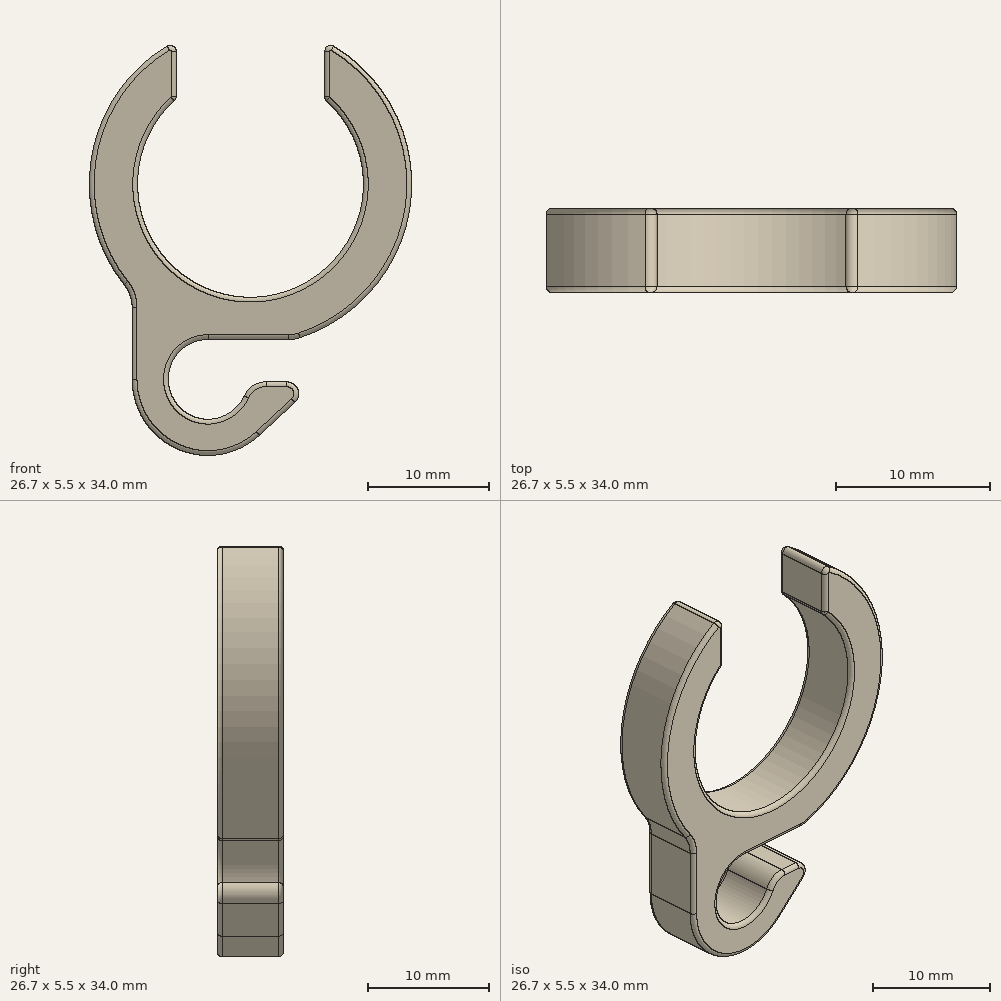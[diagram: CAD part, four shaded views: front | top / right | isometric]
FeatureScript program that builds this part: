
annotation { "Feature Type Name" : "Feature", "Feature Type Description" : "" }
export const myFeature = defineFeature(function(context is Context, id is Id, definition is map)
    precondition{}
    {
        {
            var Q0;
            Q0=qCreatedBy(makeId("Front.planeOp"),FACE);
            var sketch = newSketch(context, id + "F0", { "sketchPlane" : qUnion([Q0])});
            skArc(sketch, "E0", {"start": v(-6.31, 6.9) * mm, "mid": v(0, -9.35) * mm, "end": v(6.31, 6.9) * mm});
            skArc(sketch, "E1", {"start": v(-6.9, 11.42) * mm, "mid": v(-13.14, 2.36) * mm, "end": v(-10.45, -8.3) * mm});
            skLineSegment(sketch, "E2", {"start": v(-6.15, 11) * mm, "end": v(-6.15, 7.27) * mm});
            skLineSegment(sketch, "E3", {"start": v(6.15, 11) * mm, "end": v(6.15, 7.27) * mm});
            skPoint(sketch, "E4.visualSharp", {"position": v(-6.15, 11.85) * mm});
            skArc(sketch, "E4.filletArc", {"start": v(-6.15, 11) * mm, "mid": v(-6.4, 11.43) * mm, "end": v(-6.9, 11.42) * mm});
            skPoint(sketch, "E5.visualSharp", {"position": v(-6.15, 7.04) * mm});
            skArc(sketch, "E5.filletArc", {"start": v(-6.31, 6.9) * mm, "mid": v(-6.2, 7.06) * mm, "end": v(-6.15, 7.27) * mm});
            skPoint(sketch, "E6.visualSharp", {"position": v(6.15, 7.04) * mm});
            skArc(sketch, "E6.filletArc", {"start": v(6.15, 7.27) * mm, "mid": v(6.2, 7.06) * mm, "end": v(6.31, 6.9) * mm});
            skPoint(sketch, "E7.visualSharp", {"position": v(6.15, 11.85) * mm});
            skArc(sketch, "E7.filletArc", {"start": v(6.9, 11.42) * mm, "mid": v(6.4, 11.43) * mm, "end": v(6.15, 11) * mm});
            skLineSegment(sketch, "E8", {"start": v(0.78, -20.77) * mm, "end": v(3.68, -18.08) * mm});
            skArc(sketch, "E9", {"start": v(-3.5, -12.85) * mm, "mid": v(-6.28, -17.93) * mm, "end": v(-0.5, -17.52) * mm});
            skArc(sketch, "E10", {"start": v(-9.8, -16.15) * mm, "mid": v(-6.02, -21.92) * mm, "end": v(0.78, -20.77) * mm});
            skLineSegment(sketch, "E11", {"start": v(1.32, -16.35) * mm, "end": v(3, -16.35) * mm});
            skArc(sketch, "E12.filletArc", {"start": v(3.68, -18.08) * mm, "mid": v(3.93, -16.98) * mm, "end": v(3, -16.35) * mm});
            skLineSegment(sketch, "E13", {"start": v(-3.5, -12.85) * mm, "end": v(3.18, -12.85) * mm});
            skArc(sketch, "E14.trimOffspring", {"start": v(4.1, -12.7) * mm, "mid": v(13.26, -1.54) * mm, "end": v(6.9, 11.42) * mm});
            skLineSegment(sketch, "E15", {"start": v(-9.8, -16.15) * mm, "end": v(-9.8, -10.17) * mm});
            skPoint(sketch, "E16.visualSharp", {"position": v(-0.2, -16.35) * mm});
            skArc(sketch, "E16.filletArc", {"start": v(1.32, -16.35) * mm, "mid": v(0.24, -16.67) * mm, "end": v(-0.5, -17.52) * mm});
            skPoint(sketch, "E17.visualSharp", {"position": v(-9.8, -9.07) * mm});
            skArc(sketch, "E17.filletArc", {"start": v(-9.8, -10.17) * mm, "mid": v(-9.97, -9.18) * mm, "end": v(-10.45, -8.3) * mm});
            skLineSegment(sketch, "E18", {"start": v(4, -13.91) * mm, "end": v(4, -19.84) * mm});
            skPoint(sketch, "E19.visualSharp", {"position": v(3.62, -12.85) * mm});
            skArc(sketch, "E19.filletArc", {"start": v(3.18, -12.85) * mm, "mid": v(3.64, -12.81) * mm, "end": v(4.1, -12.7) * mm});
            skSolve(sketch);
        }
        {
            var Q0;
            Q0=makeQuery(id+"F0.imprint","IMPRINT",FACE,{"disambiguationData":[TD([[makeQuery(id+"F0.imprint","IMPRINT",EDGE,{"derivedFrom":sQuery(id+"F0.wireOp",EDGE,"E0")}),-1.0]])]});
            extrude(context, id + "F1", {"entities" : qUnion([Q0]), "depth" : 5.5 * mm, "offsetDistance" : 25 * mm});
        }
        {
            var Q0;
            Q0=makeQuery(id+"F1.opExtrude","CAP_FACE",FACE,{"disambiguationData":[OSD([sQuery(id+"F0.wireOp",EDGE,"E0"),sQuery(id+"F0.wireOp",EDGE,"E1"),sQuery(id+"F0.wireOp",EDGE,"E2"),sQuery(id+"F0.wireOp",EDGE,"E3"),sQuery(id+"F0.wireOp",EDGE,"E4.filletArc"),sQuery(id+"F0.wireOp",EDGE,"E5.filletArc"),sQuery(id+"F0.wireOp",EDGE,"E6.filletArc"),sQuery(id+"F0.wireOp",EDGE,"E7.filletArc"),sQuery(id+"F0.wireOp",EDGE,"E8"),sQuery(id+"F0.wireOp",EDGE,"E9"),sQuery(id+"F0.wireOp",EDGE,"E10"),sQuery(id+"F0.wireOp",EDGE,"E11"),sQuery(id+"F0.wireOp",EDGE,"E12.filletArc"),sQuery(id+"F0.wireOp",EDGE,"E13"),sQuery(id+"F0.wireOp",EDGE,"E14.trimOffspring"),sQuery(id+"F0.wireOp",EDGE,"E15"),sQuery(id+"F0.wireOp",EDGE,"E16.filletArc"),sQuery(id+"F0.wireOp",EDGE,"E17.filletArc"),sQuery(id+"F0.wireOp",EDGE,"E19.filletArc")])],"isStart":false});
            var Q1;
            Q1=makeQuery(id+"F1.opExtrude","CAP_FACE",FACE,{"disambiguationData":[OSD([sQuery(id+"F0.wireOp",EDGE,"E0"),sQuery(id+"F0.wireOp",EDGE,"E1"),sQuery(id+"F0.wireOp",EDGE,"E2"),sQuery(id+"F0.wireOp",EDGE,"E3"),sQuery(id+"F0.wireOp",EDGE,"E4.filletArc"),sQuery(id+"F0.wireOp",EDGE,"E5.filletArc"),sQuery(id+"F0.wireOp",EDGE,"E6.filletArc"),sQuery(id+"F0.wireOp",EDGE,"E7.filletArc"),sQuery(id+"F0.wireOp",EDGE,"E8"),sQuery(id+"F0.wireOp",EDGE,"E9"),sQuery(id+"F0.wireOp",EDGE,"E10"),sQuery(id+"F0.wireOp",EDGE,"E11"),sQuery(id+"F0.wireOp",EDGE,"E12.filletArc"),sQuery(id+"F0.wireOp",EDGE,"E13"),sQuery(id+"F0.wireOp",EDGE,"E14.trimOffspring"),sQuery(id+"F0.wireOp",EDGE,"E15"),sQuery(id+"F0.wireOp",EDGE,"E16.filletArc"),sQuery(id+"F0.wireOp",EDGE,"E17.filletArc"),sQuery(id+"F0.wireOp",EDGE,"E19.filletArc")])],"isStart":true});
            fillet(context, id + "F2", {"entities" : qUnion([Q0, Q1]), "radius" : 0.4 * mm, "tangentPropagation" : true, "allowEdgeOverflow" : false});
        }
    });
